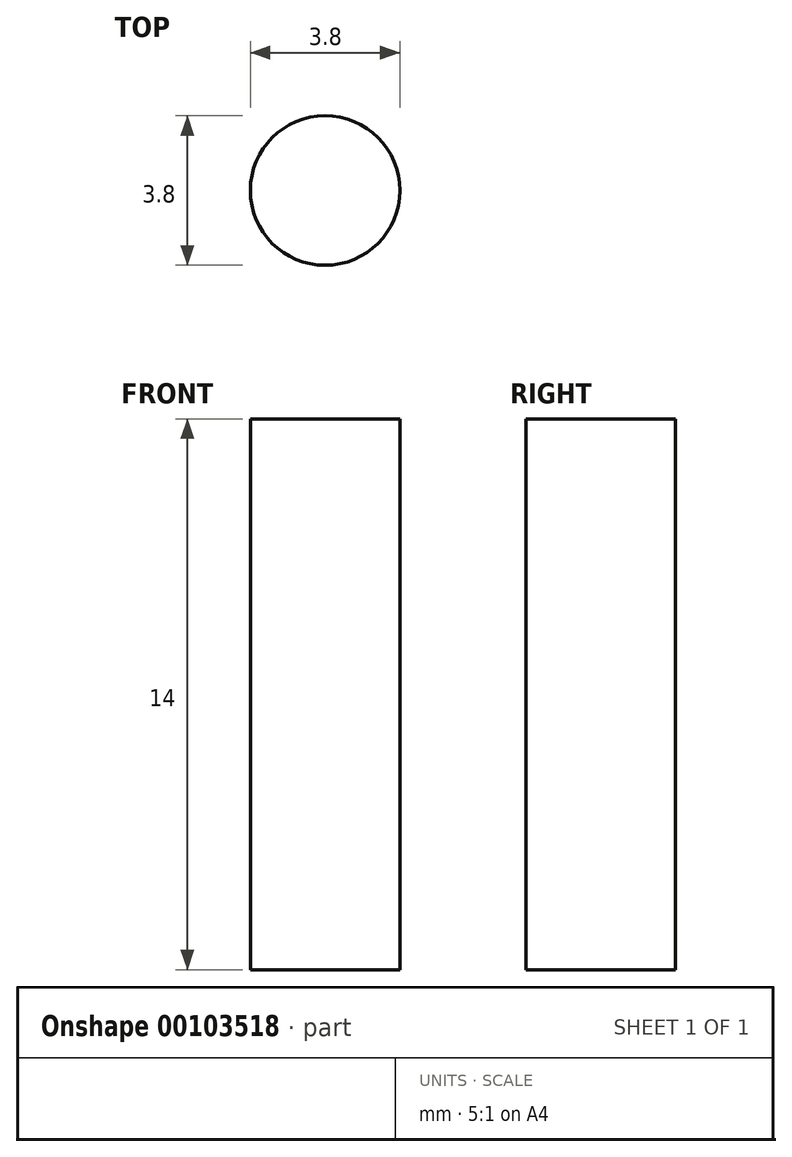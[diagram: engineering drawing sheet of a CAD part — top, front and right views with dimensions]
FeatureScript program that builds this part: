
annotation { "Feature Type Name" : "Feature", "Feature Type Description" : "" }
export const myFeature = defineFeature(function(context is Context, id is Id, definition is map)
    precondition{}
    {
        {
            var Q0;
            Q0=qCreatedBy(makeId("Top.planeOp"),FACE);
            var sketch = newSketch(context, id + "F0", { "sketchPlane" : qUnion([Q0])});
            skCircle(sketch, "E0", {"center": v(0, 0) * mm, "radius": 1.9 * mm});
            skSolve(sketch);
        }
        {
            var Q0;
            Q0 = qSketchRegion(id + "F0", true);
            extrude(context, id + "F1", {"entities" : qUnion([Q0]), "depth" : 14 * mm});
        }
    });
